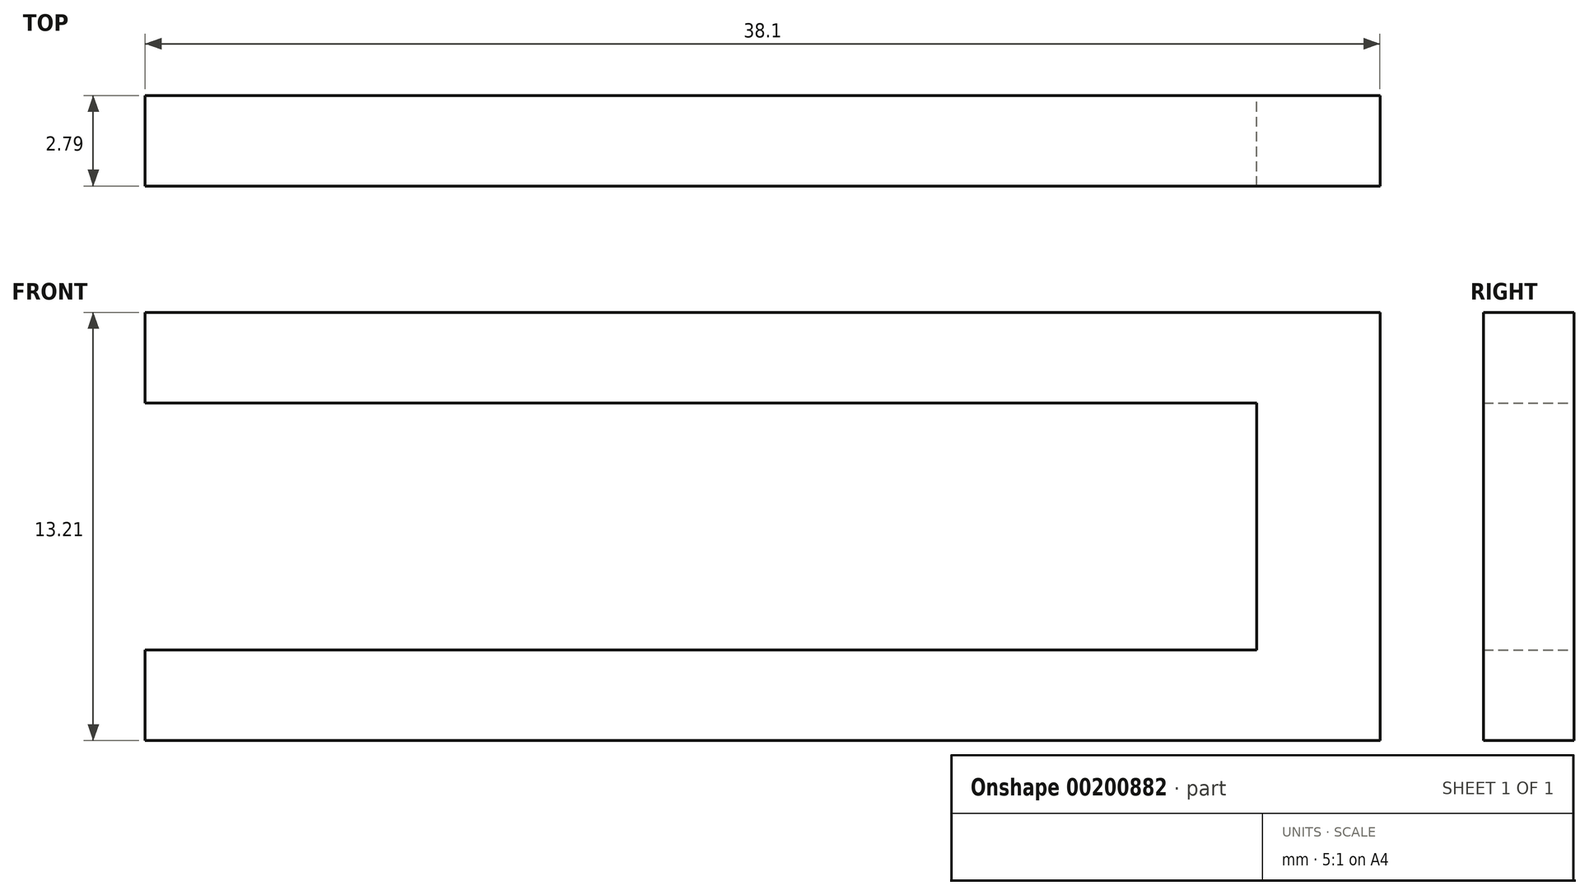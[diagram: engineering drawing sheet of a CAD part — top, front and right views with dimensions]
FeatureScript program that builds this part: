
annotation { "Feature Type Name" : "Feature", "Feature Type Description" : "" }
export const myFeature = defineFeature(function(context is Context, id is Id, definition is map)
    precondition{}
    {
        {
            var Q0;
            Q0=qCreatedBy(makeId("Front.planeOp"),FACE);
            var sketch = newSketch(context, id + "F0", { "sketchPlane" : qUnion([Q0])});
            skLineSegment(sketch, "E0", {"start": v(24.12, 3.65) * mm, "end": v(24.12, -3.97) * mm});
            skLineSegment(sketch, "E1", {"start": v(24.12, 3.65) * mm, "end": v(-10.17, 3.65) * mm});
            skLineSegment(sketch, "E2", {"start": v(24.12, -3.97) * mm, "end": v(-10.17, -3.97) * mm});
            skLineSegment(sketch, "E3", {"start": v(-10.17, 3.65) * mm, "end": v(-10.17, 6.44) * mm});
            skLineSegment(sketch, "E4", {"start": v(-10.17, 6.44) * mm, "end": v(27.93, 6.44) * mm});
            skLineSegment(sketch, "E5", {"start": v(27.93, 6.44) * mm, "end": v(27.93, -6.77) * mm});
            skLineSegment(sketch, "E6", {"start": v(27.93, -6.77) * mm, "end": v(-10.17, -6.77) * mm});
            skLineSegment(sketch, "E7", {"start": v(-10.17, -6.77) * mm, "end": v(-10.17, -3.97) * mm});
            skLineSegment(sketch, "E8", {"start": v(24.12, -0.16) * mm, "end": v(27.93, -0.16) * mm});
            skSolve(sketch);
        }
        {
            var Q0;
            Q0 = qSketchRegion(id + "F0", true);
            extrude(context, id + "F1", {"entities" : qUnion([Q0]), "depth" : 2.8 * mm});
        }
    });
